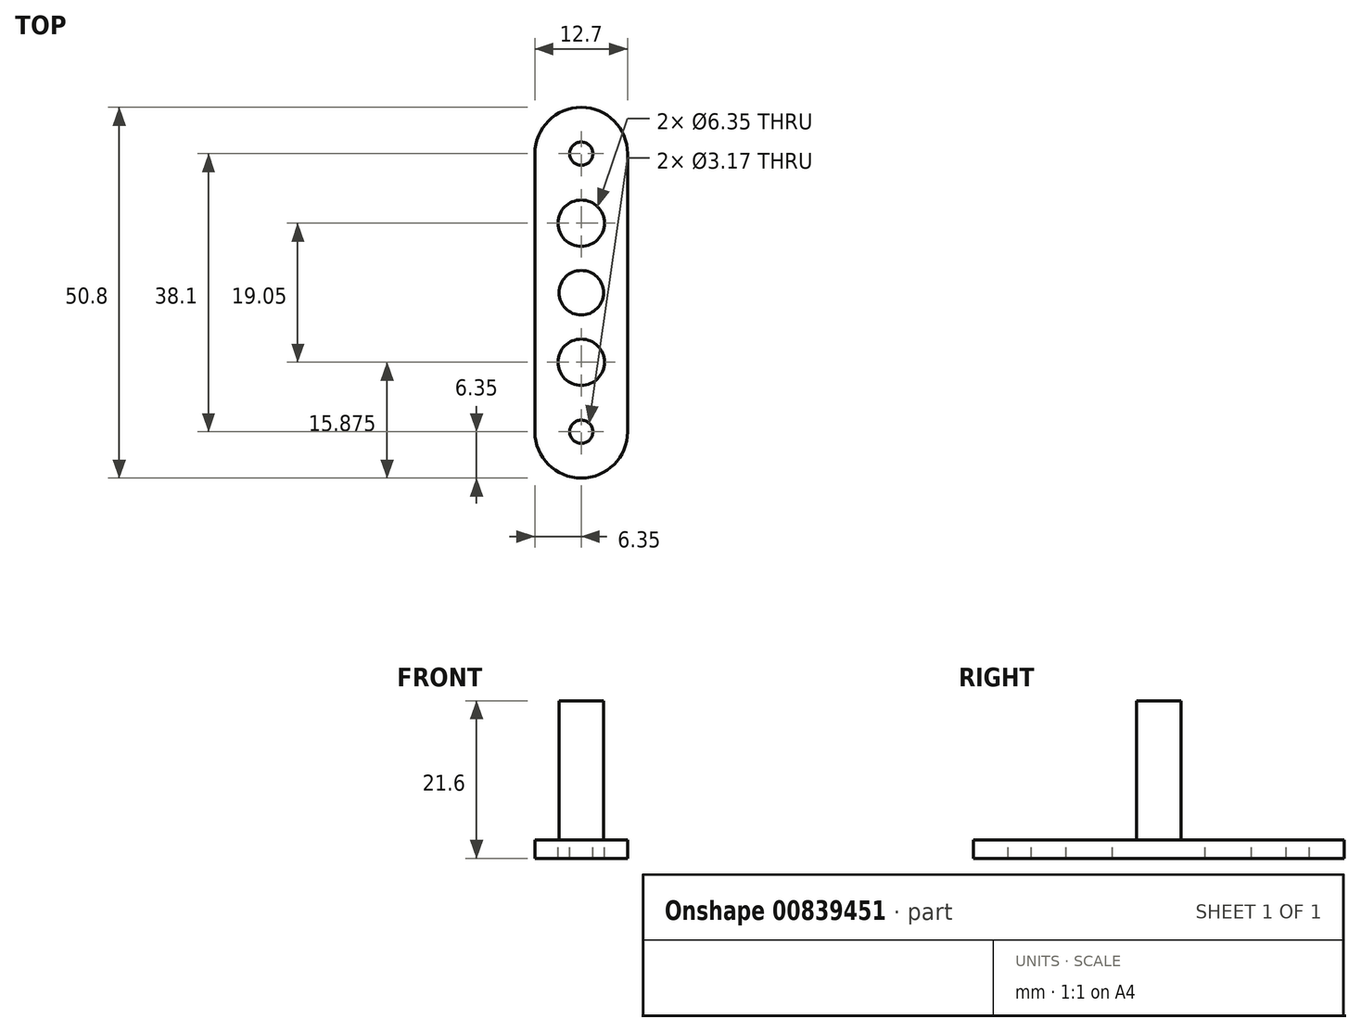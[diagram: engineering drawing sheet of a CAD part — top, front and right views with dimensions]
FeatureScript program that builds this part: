
annotation { "Feature Type Name" : "Feature", "Feature Type Description" : "" }
export const myFeature = defineFeature(function(context is Context, id is Id, definition is map)
    precondition{}
    {
        {
            var Q0;
            Q0=qCreatedBy(makeId("Top.planeOp"),FACE);
            var sketch = newSketch(context, id + "F0", { "sketchPlane" : qUnion([Q0])});
            skCircle(sketch, "E0", {"center": v(0, 0) * mm, "radius": 3.05 * mm});
            skSolve(sketch);
        }
        {
            var Q0;
            Q0 = qSketchRegion(id + "F0", true);
            extrude(context, id + "F1", {"entities" : qUnion([Q0]), "depth" : 19.05 * mm, "offsetDistance" : 25.4 * mm, "symmetric" : true});
        }
        {
            var Q0;
            Q0=makeQuery(id+"F1.opExtrude","CAP_FACE",FACE,{"disambiguationData":[OSD([sQuery(id+"F0.wireOp",EDGE,"E0")])],"isStart":true});
            var sketch = newSketch(context, id + "F2", { "sketchPlane" : qUnion([Q0])});
            skLineSegment(sketch, "E1.bottom", {"start": v(6.35, -25.4) * mm, "end": v(-6.35, -25.4) * mm});
            skLineSegment(sketch, "E1.top", {"start": v(6.35, 25.4) * mm, "end": v(-6.35, 25.4) * mm});
            skLineSegment(sketch, "E1.left", {"start": v(6.35, -25.4) * mm, "end": v(6.35, 25.4) * mm});
            skLineSegment(sketch, "E1.right", {"start": v(-6.35, -25.4) * mm, "end": v(-6.35, 25.4) * mm});
            skPoint(sketch, "E1.middle", {"position": v(0, 0) * mm});
            skSolve(sketch);
        }
        {
            var Q0;
            Q0 = qSketchRegion(id + "F2", true);
            extrude(context, id + "F3", {"entities" : qUnion([Q0]), "operationType" : NewBodyOperationType.ADD, "depth" : 2.54 * mm, "offsetDistance" : 25.4 * mm});
        }
        {
            var Q0;
            Q0=makeQuery(id+"F3.opExtrude","SWEPT_EDGE",EDGE,{"disambiguationData":[OSD([sQuery(id+"F2.wireOp",EDGE,"E1.bottom"),sQuery(id+"F2.wireOp",EDGE,"E1.right")])]});
            var Q1;
            Q1=makeQuery(id+"F3.opExtrude","SWEPT_EDGE",EDGE,{"disambiguationData":[OSD([sQuery(id+"F2.wireOp",EDGE,"E1.bottom"),sQuery(id+"F2.wireOp",EDGE,"E1.left")])]});
            var Q2;
            Q2=makeQuery(id+"F3.opExtrude","SWEPT_EDGE",EDGE,{"disambiguationData":[OSD([sQuery(id+"F2.wireOp",EDGE,"E1.top"),sQuery(id+"F2.wireOp",EDGE,"E1.right")])]});
            var Q3;
            Q3=makeQuery(id+"F3.opExtrude","SWEPT_EDGE",EDGE,{"disambiguationData":[OSD([sQuery(id+"F2.wireOp",EDGE,"E1.top"),sQuery(id+"F2.wireOp",EDGE,"E1.left")])]});
            fillet(context, id + "F4", {"entities" : qUnion([Q0, Q1, Q2, Q3]), "tangentPropagation" : true, "radius" : 6.35 * mm, "defaultsChanged" : true, "vertexSettings" : [], "allowEdgeOverflow" : false});
        }
        {
            var Q0;
            Q0=makeQuery(id+"F3.opExtrude","CAP_FACE",FACE,{"disambiguationData":[OSD([sQuery(id+"F2.wireOp",EDGE,"E1.bottom"),sQuery(id+"F2.wireOp",EDGE,"E1.top"),sQuery(id+"F2.wireOp",EDGE,"E1.left"),sQuery(id+"F2.wireOp",EDGE,"E1.right")])],"isStart":true});
            var sketch = newSketch(context, id + "F5", { "sketchPlane" : qUnion([Q0])});
            skLineSegment(sketch, "E2", {"start": v(0, 0) * mm, "end": v(0, 19.05) * mm, "construction": true});
            skCircle(sketch, "E3", {"center": v(0, 19.05) * mm, "radius": 1.59 * mm});
            skCircle(sketch, "E4", {"center": v(0, 9.53) * mm, "radius": 3.18 * mm});
            skCircle(sketch, "E5.MirrorC", {"center": v(0, -19.05) * mm, "radius": 1.59 * mm});
            skCircle(sketch, "E6.MirrorC", {"center": v(0, -9.53) * mm, "radius": 3.18 * mm});
            skSolve(sketch);
        }
        {
            var Q0;
            Q0 = qSketchRegion(id + "F5", true);
            extrude(context, id + "F6", {"entities" : qUnion([Q0]), "operationType" : NewBodyOperationType.REMOVE, "endBound" : BoundingType.THROUGH_ALL, "oppositeDirection" : true, "depth" : 25.4 * mm, "offsetDistance" : 25.4 * mm});
        }
    });
